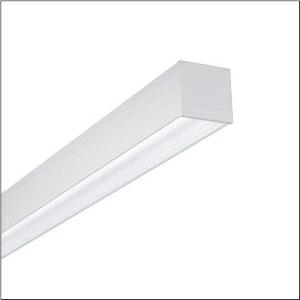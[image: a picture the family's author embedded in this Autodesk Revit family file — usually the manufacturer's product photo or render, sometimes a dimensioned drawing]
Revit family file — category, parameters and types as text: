
# Revit family: silica_r_5mx21bd2e4a_11e7
name_source: partatom
category: Lighting Fixtures
units: mm (PartAtom-declared; Revit-internal decimal feet)

## family parameters
Cut with Voids When Loaded = No
Host = Face
Light Source = No
Part Type = Normal
Room Calculation Point = No
Round Connector Dimension = Use Diameter
Shared = No

## types (1)
- --- (1 x LED, 9910 lm, 60.1 W, 4000K)
    Apparent Load = 60 VA
    CIE Flux Codes = 82 97 100 100 100
    Color Rendering = 80
    Color Temperature = 4000K
    Default Elevation = 1800 mm
    Description = Silica®, office luminaire, of aluminium, light emission: direct distribution, primary light characteristic: symmetric, installation type: surface-mounted, LED rated luminous flux: 9.910 lm, light colour: 840, colour temperature: 4000K, control gear: ECG DALI, with terminal, 3+2-pole, max. 2.5mm², mains connection: 230V, AC, 50/60Hz, rated input power: 60W, luminaire housing, of aluminium, anodised, silver, length: 2.880 mm, width: 64 mm, height: 64mm, protection rating (complete): IP20, insulation class (complete): insulation class I (protective earthing), certification: CE, permissible ambient temperature for indoor applications: 0..+35°C, standard: EN 50419, packaging unit: 1 piece
    Height = 64 mm
    Lamp = 1 x LED
    Lamp Light Flux = 9910 lm
    Lamp Power = 60.1 W
    Lamp count = 1
    Length = 2845 mm
    Luminous efficacy = 165 lm/W
    Manufacturer = Siteco
    ModVariant = No
    Model = 5MX21BD2E4A
    Mounting Place = Ceiling
    Mounting Type = Surface mounted
    Number of Poles = 1
    OnlyDefault = Yes
    Power Factor = 1
    Product Name = Silica®
    Product group = office luminaire | ceiling mounted
    ProductGroupID = 302
    Protection Class = Protection class I
    Protection Degree = IP 20
    RLX_Detail_Level = 1
    RlxData = <blob elided: 27177 chars, md5=5a1f64b7>
    Socket = socket
    Standby Power = 0 W
    System Light Flux = 9910 lm
    System Power = 60 W
    Type Comments = factory setting: luminous flux: 100 % | dim-lin: 254 | 336 mA
    Type Image = l_1004827.jpg
    URL = http://relux.com
    VarID = @adj_132148
    Voltage = 0 V
    Weight = 0.00 kg
    Width = 66 mm

## geometry (parser evidence)
native form markers: Blend x4, Sweep x10
no freeform markers — native parametric forms only
